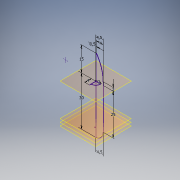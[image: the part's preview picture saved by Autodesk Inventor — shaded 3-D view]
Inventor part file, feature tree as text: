
AUTODESK INVENTOR PART (.ipt)
format: ipt  version: 2016 (Build 200138000, 138)  size: 99,840 bytes
history: native  units: mm
features: plane x6, sketch x3
ambient origin geometry x8: Origin, YZ Plane, XZ Plane, XY Plane, X Axis, Y Axis, Z Axis, Center Point
feature tree (9):
  sketch  "Sketch1"  dims[d1=0.5mm]
  sketch  "Sketch2"  dims[d2=2.0mm]
  plane  "Work Plane1"
  plane  "Work Plane3"
  plane  "Work Plane6"
  sketch  "Sketch3"  dims[d4=25.0mm d5=4.0mm d6=15.0mm d7=30.0mm d8=4.5mm d14=4.5mm d15=8.0mm d16=4.0mm d17=-20.0mm d18=-2.0mm d19=-2.0mm d20=4.0mm d24=3.0mm]
  plane  "Work Plane2"
  plane  "Work Plane4"
  plane  "Work Plane5"
